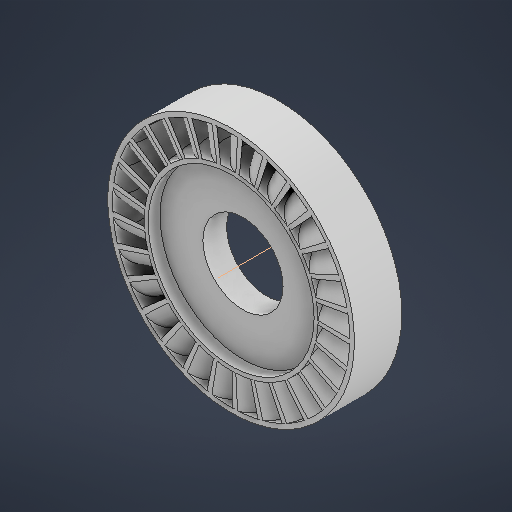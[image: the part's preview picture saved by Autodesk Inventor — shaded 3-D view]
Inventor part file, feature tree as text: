
AUTODESK INVENTOR PART (.ipt)
format: ipt  version: 2025.3 (Build 293356030, 356C)  size: 540,160 bytes
history: native  units: mm
features: extrude x5, sketch x4, sweep x1, pattern_circular x1, other x1
ambient origin geometry x8: Origin, YZ Plane, XZ Plane, XY Plane, X Axis, Y Axis, Z Axis, Center Point
bodies: Solid1 (feature_tree)
feature tree (12):
  sketch  "Sketch1"  dims[d0=36.6mm d1=50.0mm]
  extrude  "Extrusion1"  Depth=50.0mm
  extrude  "Extrusion2"  Depth=10.0mm TaperAngle=0.0deg
  sketch  "Sketch2"  dims[d2=5.0mm d3=0.0mm d4=10.0mm d5=0.0mm]
  sweep  "Sweep1"
  pattern_circular  "Circular Pattern1"  Count=29 Angle=360.0deg
  extrude  "Extrusion3"  Depth=10.0mm
  extrude  "Extrusion4"  Depth=10.0mm
  extrude  "Extrusion5"  Depth=10.0mm TaperAngle=0.0deg
  other  "Work Axis1"
  sketch  "Sketch7"  dims[d6=1.745329mm d7=0.0mm d8=0.0mm]
  sketch  "Sketch8"  dims[d10=1.0mm d11=290.0mm d12=360.0deg d14=35.0mm d15=52.0mm d16=10.0mm d17=0.0mm d18=10.0mm d19=0.0mm d20=16.9mm d21=0.0mm d22=0.0mm]
